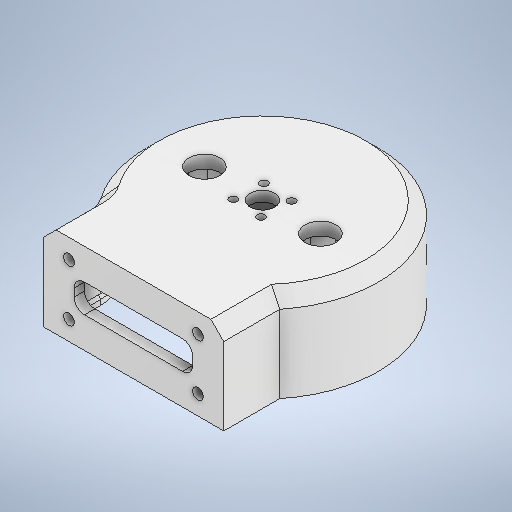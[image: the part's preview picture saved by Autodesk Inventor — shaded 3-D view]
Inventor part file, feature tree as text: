
AUTODESK INVENTOR PART (.ipt)
format: ipt  version: 2025.2 (Build 292293000, 293)  size: 643,072 bytes
history: native  units: mm
features: extrude x7, sketch x6, fillet x3, plane x2, chamfer x1, shell x1, pattern_circular x1, sweep x1, revolve x1, projected_geometry x1
ambient origin geometry x8: Origin, YZ Plane, XZ Plane, XY Plane, X Axis, Y Axis, Z Axis, Center Point
bodies: Solid1 (feature_tree)
feature tree (24):
  sketch  "Sketch1"  dims[d0=45.0deg d1=23.044078mm d2=34.0mm d3=6.0mm d4=8.0mm d5=11.0mm d6=12.0mm d7=18.0mm d8=16.6mm d9=12.5mm d10=1.0mm d11=10.0mm]
  extrude  "Extrusion1"  TaperAngle=45.0deg  [1 undecoded]
  extrude  "Extrusion2"  Depth=34.0mm
  fillet  "Fillet1"  Radius=45.0mm
  chamfer  "Chamfer1"  Distance=30.0mm
  shell  "Shell2"  Thickness=5.0mm
  sketch  "Sketch2"  dims[d13=22.0mm d16=8.0mm d17=11.0mm d19=18.0mm d20=16.6mm d22=1.0mm d24=45.0deg]
  extrude  "Extrusion9"  Depth=4.0mm
  extrude  "Extrusion10"  Depth=5.0mm TaperAngle=0.0deg
  extrude  "Extrusion3"  Depth=4.0mm TaperAngle=360.0deg
  pattern_circular  "Circular Pattern1"  [2 undecoded]
  extrude  "Extrusion11"  Depth=4.0mm
  plane  "Work Plane2"
  sketch  "Sketch5"  dims[d25=22.0mm d26=34.0mm d27=45.0mm]
  plane  "Work Plane3"
  sweep  "Sweep1"
  extrude  "Extrusion12"  TaperAngle=45.0deg  [1 undecoded]
  revolve  "Revolution1"  [1 undecoded]
  fillet  "Fillet2"  Radius=22.5mm
  fillet  "Fillet3"  Radius=4.2mm
  sketch  "Sketch6"  dims[d28=90.0mm d29=30.0mm d30=0.0mm d32=5.0mm d33=0.0mm]
  sketch  "Sketch7"  dims[d34=4.0mm d35=3.1mm]
  projected_geometry  "Projected Loop1"
  sketch  "Sketch8"  dims[d36=8.0mm d37=5.0mm d38=0.0mm d39=40.0mm d40=360.0deg d42=12.0mm d48=70.0mm d49=50.0mm d50=45.0deg d58=10.0mm d73=22.5mm d74=4.2mm d75=0.0mm d76=9.5mm d77=0.0mm d78=0.0mm d79=0.0mm d80=-3.0mm d81=45.0deg d82=1.0mm d83=0.0mm d84=0.0mm d85=12.0mm d86=20.0mm d87=50.0mm d88=4.2mm d89=20.0mm d90=0.0mm d91=0.1mm d92=0.1mm d93=9.5mm d94=5.0mm d95=2.0mm d96=45.0deg d97=90.0deg d98=6.0mm d99=10.0mm d100=3.0mm d101=4.0mm]
note: 5 required parameter values undecoded (feature->parameter linkage not recoverable at this tier; creation-order binding heuristic only, values carry confidence <= 0.55)